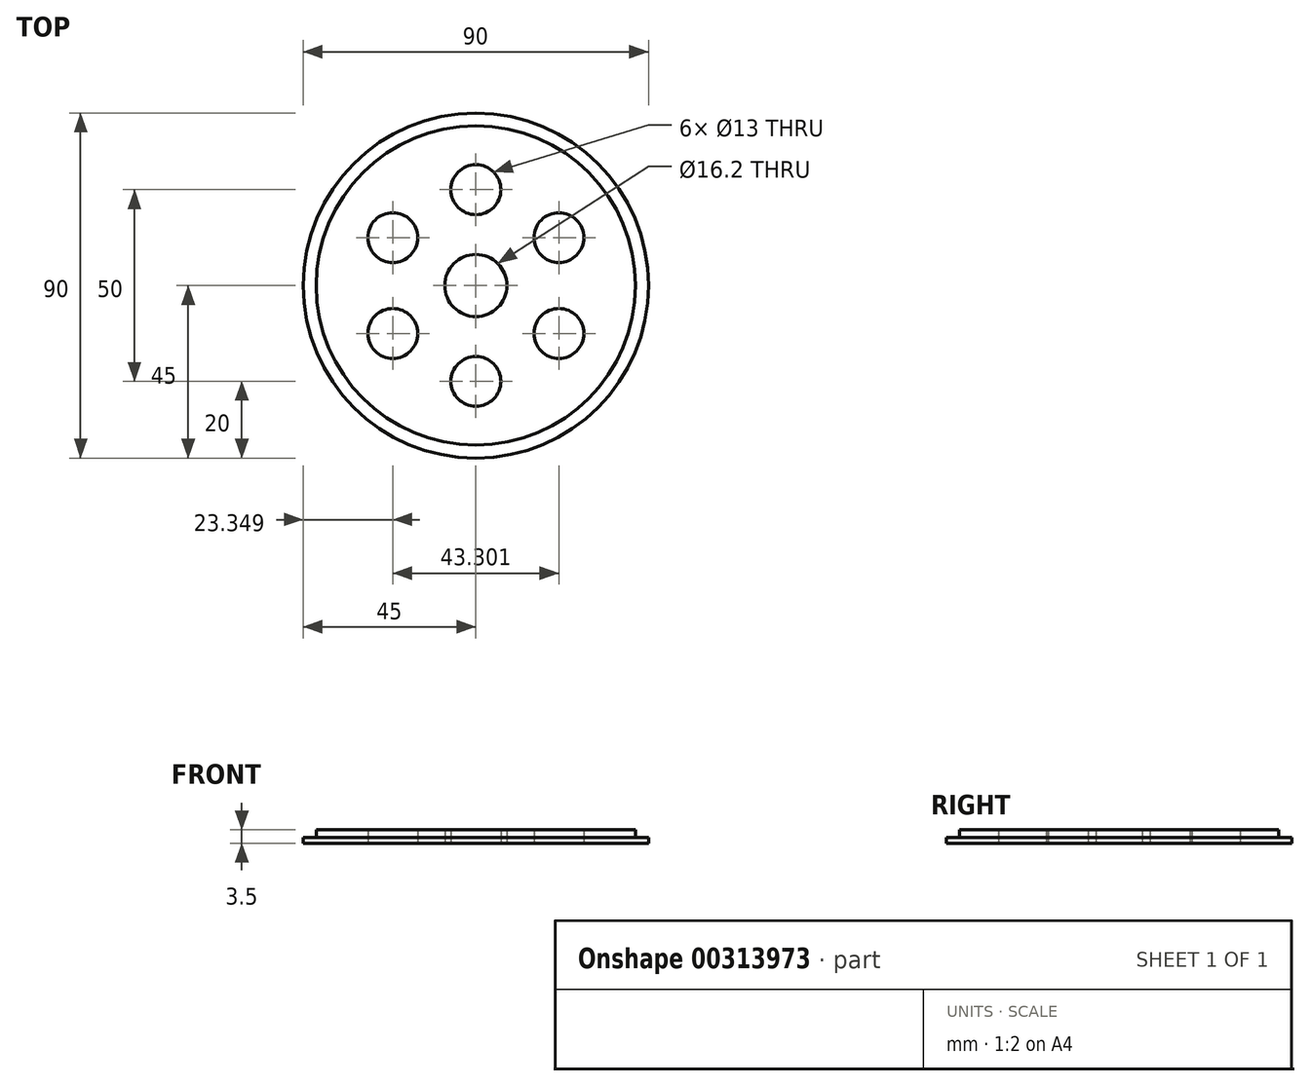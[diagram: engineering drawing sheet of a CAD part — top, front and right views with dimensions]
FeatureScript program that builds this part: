
annotation { "Feature Type Name" : "Feature", "Feature Type Description" : "" }
export const myFeature = defineFeature(function(context is Context, id is Id, definition is map)
    precondition{}
    {
        {
            var Q0;
            Q0=qCreatedBy(makeId("Top.planeOp"),FACE);
            var sketch = newSketch(context, id + "F0", { "sketchPlane" : qUnion([Q0])});
            skCircle(sketch, "E0", {"center": v(0, 0) * mm, "radius": 41.62 * mm});
            skCircle(sketch, "E1", {"center": v(0, 0) * mm, "radius": 8.1 * mm});
            skCircle(sketch, "E2", {"center": v(0, 0) * mm, "radius": 45 * mm});
            skCircle(sketch, "E3.cCircle", {"center": v(0, 0) * mm, "radius": 21.65 * mm, "construction": true});
            skLineSegment(sketch, "E3.0", {"start": v(0, 25) * mm, "end": v(21.65, 12.5) * mm});
            skLineSegment(sketch, "E3.1", {"start": v(21.65, 12.5) * mm, "end": v(21.65, -12.5) * mm});
            skLineSegment(sketch, "E3.2", {"start": v(21.65, -12.5) * mm, "end": v(0, -25) * mm});
            skLineSegment(sketch, "E3.3", {"start": v(0, -25) * mm, "end": v(-21.65, -12.5) * mm});
            skLineSegment(sketch, "E3.4", {"start": v(-21.65, -12.5) * mm, "end": v(-21.65, 12.5) * mm});
            skLineSegment(sketch, "E3.5", {"start": v(-21.65, 12.5) * mm, "end": v(0, 25) * mm});
            skPoint(sketch, "E3.0.midPoint", {"position": v(10.83, 18.75) * mm});
            skCircle(sketch, "E4", {"center": v(0, 25) * mm, "radius": 6.5 * mm});
            skCircle(sketch, "E5", {"center": v(21.65, 12.5) * mm, "radius": 6.5 * mm});
            skCircle(sketch, "E6", {"center": v(21.65, -12.5) * mm, "radius": 6.5 * mm});
            skCircle(sketch, "E7", {"center": v(0, -25) * mm, "radius": 6.5 * mm});
            skCircle(sketch, "E8", {"center": v(-21.65, -12.5) * mm, "radius": 6.5 * mm});
            skCircle(sketch, "E9", {"center": v(-21.65, 12.5) * mm, "radius": 6.5 * mm});
            skSolve(sketch);
        }
        {
            var Q0;
            Q0=makeQuery(id+"F0.imprint","IMPRINT",FACE,{"disambiguationData":[TD([[makeQuery(id+"F0.imprint","IMPRINT",EDGE,{"derivedFrom":sQuery(id+"F0.wireOp",EDGE,"E0")}),1.0]])]});
            var Q1;
            Q1=makeQuery(id+"F0.imprint","IMPRINT",FACE,{"disambiguationData":[TD([[makeQuery(id+"F0.imprint","IMPRINT",EDGE,{"derivedFrom":sQuery(id+"F0.wireOp",EDGE,"E1")}),-1.0]])]});
            extrude(context, id + "F1", {"entities" : qUnion([Q0, Q1]), "depth" : 3.5 * mm});
        }
        {
            var Q0;
            Q0=makeQuery(id+"F0.imprint","IMPRINT",FACE,{"disambiguationData":[TD([[makeQuery(id+"F0.imprint","IMPRINT",EDGE,{"derivedFrom":sQuery(id+"F0.wireOp",EDGE,"E0")}),-1.0]])]});
            extrude(context, id + "F2", {"entities" : qUnion([Q0]), "operationType" : NewBodyOperationType.ADD, "depth" : 1.5 * mm});
        }
    });
